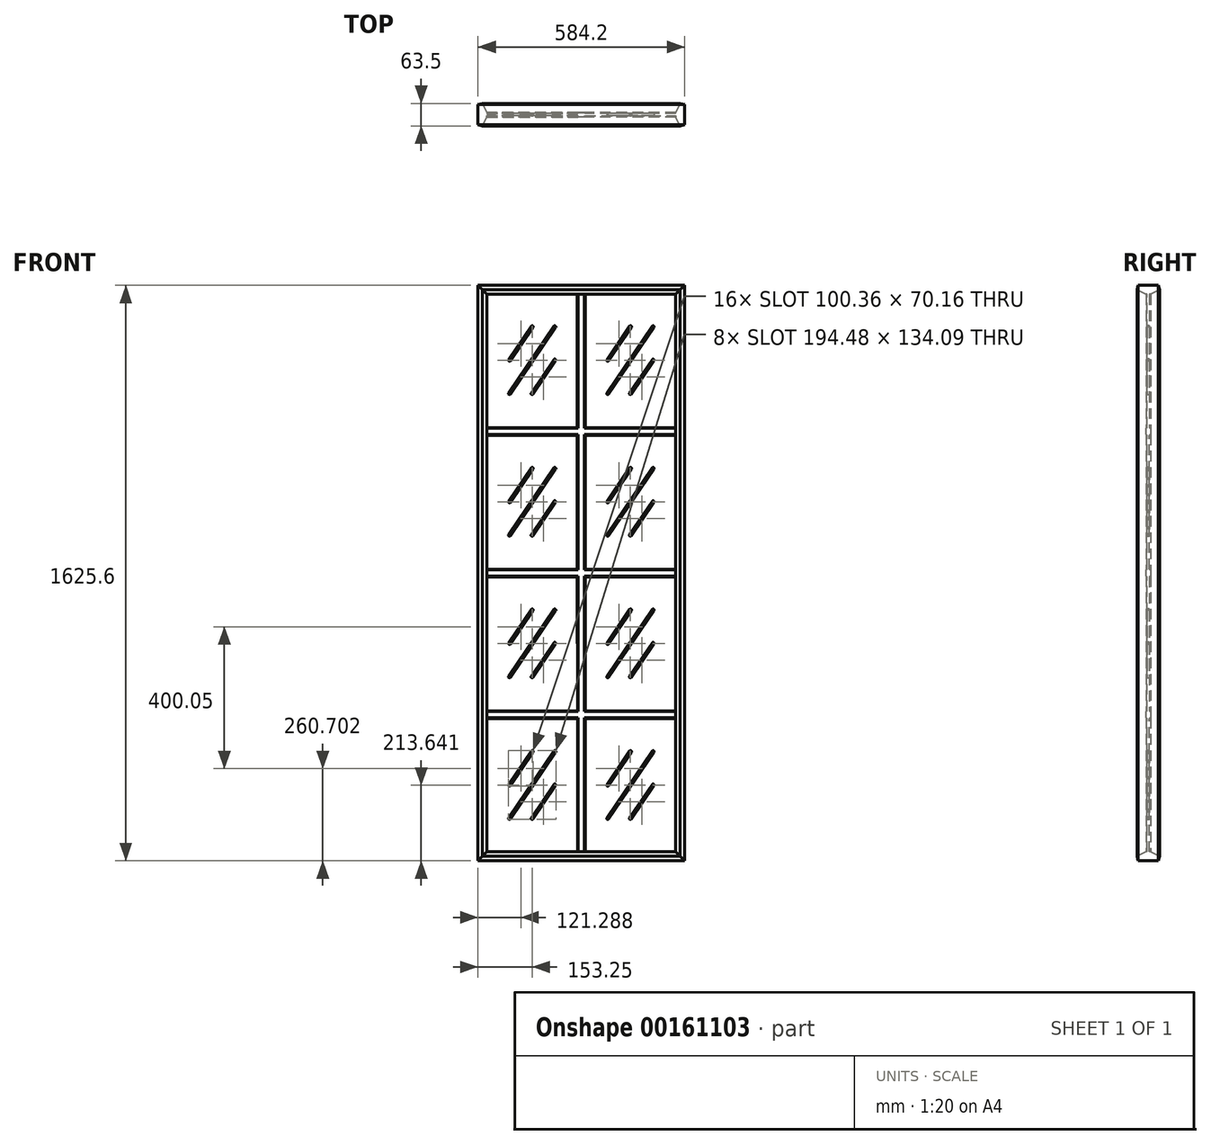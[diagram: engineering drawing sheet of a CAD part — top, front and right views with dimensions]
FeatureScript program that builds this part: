
annotation { "Feature Type Name" : "Feature", "Feature Type Description" : "" }
export const myFeature = defineFeature(function(context is Context, id is Id, definition is map)
    precondition{}
    {
        {
            var Q0;
            Q0=qCreatedBy(makeId("Front.planeOp"),FACE);
            var sketch = newSketch(context, id + "F0", { "sketchPlane" : qUnion([Q0])});
            skLineSegment(sketch, "E0.bottom", {"start": v(292.1, 812.8) * mm, "end": v(-292.1, 812.8) * mm});
            skLineSegment(sketch, "E0.top", {"start": v(292.1, -812.8) * mm, "end": v(-292.1, -812.8) * mm});
            skLineSegment(sketch, "E0.left", {"start": v(292.1, 812.8) * mm, "end": v(292.1, -812.8) * mm});
            skLineSegment(sketch, "E0.right", {"start": v(-292.1, 812.8) * mm, "end": v(-292.1, -812.8) * mm});
            skPoint(sketch, "E0.middle", {"position": v(0, 0) * mm});
            skSolve(sketch);
        }
        {
            var Q0;
            Q0 = qSketchRegion(id + "F0", true);
            var Q1;
            Q1 = qConstructionFilter(qBodyType(qCreatedBy(id + "F0" ,EDGE), BodyType.WIRE), ConstructionObject.NO);
            extrude(context, id + "F1", {"entities" : qUnion([Q0]), "bodyType" : ToolBodyType.SURFACE, "surfaceEntities" : qUnion([Q1]), "depth" : 28.57 * mm, "hasSecondDirection" : true, "secondDirectionOppositeDirection" : true, "secondDirectionDepth" : 28.57 * mm});
        }
        {
            var Q0;
            Q0=qCreatedBy(makeId("Front.planeOp"),FACE);
            var sketch = newSketch(context, id + "F2", { "sketchPlane" : qUnion([Q0])});
            skLineSegment(sketch, "E1.bottom", {"start": v(279.4, 800.1) * mm, "end": v(-279.4, 800.1) * mm});
            skLineSegment(sketch, "E1.top", {"start": v(279.4, -800.1) * mm, "end": v(-279.4, -800.1) * mm});
            skLineSegment(sketch, "E1.left", {"start": v(279.4, 800.1) * mm, "end": v(279.4, -800.1) * mm});
            skLineSegment(sketch, "E1.right", {"start": v(-279.4, 800.1) * mm, "end": v(-279.4, -800.1) * mm});
            skPoint(sketch, "E1.middle", {"position": v(0, 0) * mm});
            skSolve(sketch);
        }
        {
            var Q0;
            Q0 = qSketchRegion(id + "F2", true);
            var Q1;
            Q1 = qConstructionFilter(qBodyType(qCreatedBy(id + "F2" ,EDGE), BodyType.WIRE), ConstructionObject.NO);
            extrude(context, id + "F3", {"entities" : qUnion([Q0]), "bodyType" : ToolBodyType.SURFACE, "surfaceEntities" : qUnion([Q1]), "depth" : 31.75 * mm, "hasSecondDirection" : true, "secondDirectionOppositeDirection" : true, "secondDirectionDepth" : 31.75 * mm});
        }
        {
            var Q0;
            Q0=makeQuery(id+"F1.opExtrude","SWEPT_FACE",FACE,{"disambiguationData":[OSD([sQuery(id+"F0.wireOp",EDGE,"E0.bottom")])]});
            var Q1;
            Q1=makeQuery(id+"F3.opExtrude","SWEPT_FACE",FACE,{"disambiguationData":[OSD([sQuery(id+"F2.wireOp",EDGE,"E1.bottom")])]});
            loft(context, id + "F4", {"sheetProfilesArray" : [{ "sheetProfileEntities" : qUnion([Q0]) }, { "sheetProfileEntities" : qUnion([Q1]) }]});
        }
        {
            var Q1;
            Q1=makeQuery(id+"F1.opExtrude","SWEPT_FACE",FACE,{"disambiguationData":[OSD([sQuery(id+"F0.wireOp",EDGE,"E0.right")])]});
            var Q2;
            Q2=makeQuery(id+"F3.opExtrude","SWEPT_FACE",FACE,{"disambiguationData":[OSD([sQuery(id+"F2.wireOp",EDGE,"E1.right")])]});
            loft(context, id + "F5", {"operationType" : NewBodyOperationType.ADD, "sheetProfilesArray" : [{ "sheetProfileEntities" : qUnion([Q1]) }, { "sheetProfileEntities" : qUnion([Q2]) }]});
        }
        {
            var Q1;
            Q1=makeQuery(id+"F3.opExtrude","SWEPT_FACE",FACE,{"disambiguationData":[OSD([sQuery(id+"F2.wireOp",EDGE,"E1.left")])]});
            var Q2;
            Q2=makeQuery(id+"F1.opExtrude","SWEPT_FACE",FACE,{"disambiguationData":[OSD([sQuery(id+"F0.wireOp",EDGE,"E0.left")])]});
            loft(context, id + "F6", {"operationType" : NewBodyOperationType.ADD, "sheetProfilesArray" : [{ "sheetProfileEntities" : qUnion([Q1]) }, { "sheetProfileEntities" : qUnion([Q2]) }]});
        }
        {
            var Q1;
            Q1=makeQuery(id+"F3.opExtrude","SWEPT_FACE",FACE,{"disambiguationData":[OSD([sQuery(id+"F2.wireOp",EDGE,"E1.top")])]});
            var Q2;
            Q2=makeQuery(id+"F1.opExtrude","SWEPT_FACE",FACE,{"disambiguationData":[OSD([sQuery(id+"F0.wireOp",EDGE,"E0.top")])]});
            loft(context, id + "F7", {"operationType" : NewBodyOperationType.ADD, "sheetProfilesArray" : [{ "sheetProfileEntities" : qUnion([Q1]) }, { "sheetProfileEntities" : qUnion([Q2]) }]});
        }
        {
            var Q0;
            Q0=qCreatedBy(makeId("Front.planeOp"),FACE);
            var sketch = newSketch(context, id + "F8", { "sketchPlane" : qUnion([Q0])});
            skLineSegment(sketch, "E2.bottom", {"start": v(266.7, 787.4) * mm, "end": v(-266.7, 787.4) * mm});
            skLineSegment(sketch, "E2.top", {"start": v(266.7, -787.4) * mm, "end": v(-266.7, -787.4) * mm});
            skLineSegment(sketch, "E2.left", {"start": v(266.7, 787.4) * mm, "end": v(266.7, -787.4) * mm});
            skLineSegment(sketch, "E2.right", {"start": v(-266.7, 787.4) * mm, "end": v(-266.7, -787.4) * mm});
            skPoint(sketch, "E2.middle", {"position": v(0, 0) * mm});
            skSolve(sketch);
        }
        {
            var Q0;
            Q0 = qSketchRegion(id + "F8", true);
            var Q1;
            Q1 = qConstructionFilter(qBodyType(qCreatedBy(id + "F8" ,EDGE), BodyType.WIRE), ConstructionObject.NO);
            extrude(context, id + "F9", {"entities" : qUnion([Q0]), "bodyType" : ToolBodyType.SURFACE, "surfaceEntities" : qUnion([Q1]), "depth" : 6.35 * mm, "hasSecondDirection" : true, "secondDirectionOppositeDirection" : true, "secondDirectionDepth" : 6.35 * mm});
        }
        {
            var Q1;
            Q1=makeQuery(id+"F3.opExtrude","SWEPT_FACE",FACE,{"disambiguationData":[OSD([sQuery(id+"F2.wireOp",EDGE,"E1.bottom")])]});
            var Q2;
            Q2=makeQuery(id+"F9.opExtrude","SWEPT_FACE",FACE,{"disambiguationData":[OSD([sQuery(id+"F8.wireOp",EDGE,"E2.bottom")])]});
            loft(context, id + "F10", {"operationType" : NewBodyOperationType.ADD, "sheetProfilesArray" : [{ "sheetProfileEntities" : qUnion([Q1]) }, { "sheetProfileEntities" : qUnion([Q2]) }]});
        }
        {
            var Q1;
            Q1=makeQuery(id+"F9.opExtrude","SWEPT_FACE",FACE,{"disambiguationData":[OSD([sQuery(id+"F8.wireOp",EDGE,"E2.right")])]});
            var Q2;
            Q2=makeQuery(id+"F3.opExtrude","SWEPT_FACE",FACE,{"disambiguationData":[OSD([sQuery(id+"F2.wireOp",EDGE,"E1.right")])]});
            loft(context, id + "F11", {"operationType" : NewBodyOperationType.ADD, "sheetProfilesArray" : [{ "sheetProfileEntities" : qUnion([Q1]) }, { "sheetProfileEntities" : qUnion([Q2]) }]});
        }
        {
            var Q1;
            Q1=makeQuery(id+"F3.opExtrude","SWEPT_FACE",FACE,{"disambiguationData":[OSD([sQuery(id+"F2.wireOp",EDGE,"E1.left")])]});
            var Q2;
            Q2=makeQuery(id+"F9.opExtrude","SWEPT_FACE",FACE,{"disambiguationData":[OSD([sQuery(id+"F8.wireOp",EDGE,"E2.left")])]});
            loft(context, id + "F12", {"operationType" : NewBodyOperationType.ADD, "sheetProfilesArray" : [{ "sheetProfileEntities" : qUnion([Q1]) }, { "sheetProfileEntities" : qUnion([Q2]) }]});
        }
        {
            var Q1;
            Q1=makeQuery(id+"F3.opExtrude","SWEPT_FACE",FACE,{"disambiguationData":[OSD([sQuery(id+"F2.wireOp",EDGE,"E1.top")])]});
            var Q2;
            Q2=makeQuery(id+"F9.opExtrude","SWEPT_FACE",FACE,{"disambiguationData":[OSD([sQuery(id+"F8.wireOp",EDGE,"E2.top")])]});
            loft(context, id + "F13", {"operationType" : NewBodyOperationType.ADD, "sheetProfilesArray" : [{ "sheetProfileEntities" : qUnion([Q1]) }, { "sheetProfileEntities" : qUnion([Q2]) }]});
        }
        {
            var Q0;
            Q0=qCreatedBy(makeId("Front.planeOp"),FACE);
            var sketch = newSketch(context, id + "F14", { "sketchPlane" : qUnion([Q0])});
            skLineSegment(sketch, "E3.0.0", {"start": v(-266.7, 787.4) * mm, "end": v(266.7, 787.4) * mm});
            skLineSegment(sketch, "E3.0.2", {"start": v(-266.7, 787.4) * mm, "end": v(266.7, 787.4) * mm});
            skLineSegment(sketch, "E4.0.0", {"start": v(266.7, -787.4) * mm, "end": v(266.7, 787.4) * mm});
            skLineSegment(sketch, "E4.0.2", {"start": v(266.7, 787.4) * mm, "end": v(266.7, -787.4) * mm});
            skLineSegment(sketch, "E5.0.0", {"start": v(-266.7, -787.4) * mm, "end": v(-266.7, 787.4) * mm});
            skLineSegment(sketch, "E5.0.2", {"start": v(-266.7, -787.4) * mm, "end": v(-266.7, 787.4) * mm});
            skLineSegment(sketch, "E6.0.0", {"start": v(-266.7, -787.4) * mm, "end": v(266.7, -787.4) * mm});
            skLineSegment(sketch, "E6.0.2", {"start": v(266.7, -787.4) * mm, "end": v(-266.7, -787.4) * mm});
            skSolve(sketch);
        }
        {
            var Q0;
            Q0 = qSketchRegion(id + "F14", true);
            extrude(context, id + "F15", {"entities" : qUnion([Q0]), "operationType" : NewBodyOperationType.ADD, "depth" : 3.17 * mm, "hasSecondDirection" : true, "secondDirectionOppositeDirection" : true, "secondDirectionDepth" : 3.17 * mm});
        }
        {
            var Q0;
            Q0=qCreatedBy(makeId("Front.planeOp"),FACE);
            var sketch = newSketch(context, id + "F16", { "sketchPlane" : qUnion([Q0])});
            skLineSegment(sketch, "E7", {"start": v(0, -796.3) * mm, "end": v(-12.7, -796.3) * mm});
            skLineSegment(sketch, "E8", {"start": v(-12.7, -796.3) * mm, "end": v(-13.25, 796.46) * mm});
            skLineSegment(sketch, "E9", {"start": v(-13.25, 796.46) * mm, "end": v(-0.76, 796.46) * mm});
            skLineSegment(sketch, "E10", {"start": v(-0.76, 796.46) * mm, "end": v(12.7, 796.46) * mm});
            skLineSegment(sketch, "E11", {"start": v(12.7, 796.46) * mm, "end": v(12.7, -796.3) * mm});
            skLineSegment(sketch, "E12", {"start": v(12.7, -796.3) * mm, "end": v(0, -796.3) * mm});
            skSolve(sketch);
        }
        {
            var Q0;
            Q0 = qSketchRegion(id + "F16", true);
            extrude(context, id + "F17", {"entities" : qUnion([Q0]), "operationType" : NewBodyOperationType.ADD, "depth" : 6.35 * mm, "hasDraft" : true, "draftAngle" : 30 * degree, "draftPullDirection" : true, "hasSecondDirection" : true, "secondDirectionOppositeDirection" : true, "secondDirectionDepth" : 6.35 * mm, "hasSecondDirectionDraft" : true, "secondDirectionDraftAngle" : 30 * degree, "secondDirectionDraftPullDirection" : true});
        }
        {
            var Q0;
            Q0=qCreatedBy(makeId("Front.planeOp"),FACE);
            var sketch = newSketch(context, id + "F18", { "sketchPlane" : qUnion([Q0])});
            skLineSegment(sketch, "E13", {"start": v(-282.62, -412.75) * mm, "end": v(-282.62, -387.35) * mm});
            skLineSegment(sketch, "E14", {"start": v(-282.62, -387.35) * mm, "end": v(278.66, -387.35) * mm});
            skLineSegment(sketch, "E15", {"start": v(278.66, -387.35) * mm, "end": v(278.66, -412.75) * mm});
            skLineSegment(sketch, "E16", {"start": v(278.66, -412.75) * mm, "end": v(-282.62, -412.75) * mm});
            skLineSegment(sketch, "E17", {"start": v(-282.62, 12.7) * mm, "end": v(-282.62, -12.7) * mm});
            skLineSegment(sketch, "E18", {"start": v(-282.62, -12.7) * mm, "end": v(278.66, -12.7) * mm});
            skLineSegment(sketch, "E19", {"start": v(278.66, -12.7) * mm, "end": v(278.66, 12.7) * mm});
            skLineSegment(sketch, "E20", {"start": v(278.66, 12.7) * mm, "end": v(-282.62, 12.7) * mm});
            skLineSegment(sketch, "E21", {"start": v(-282.62, -387.35) * mm, "end": v(-282.62, -412.75) * mm});
            skLineSegment(sketch, "E22", {"start": v(-282.62, 387.35) * mm, "end": v(-282.62, 412.75) * mm});
            skLineSegment(sketch, "E23", {"start": v(-282.62, 412.75) * mm, "end": v(278.66, 412.75) * mm});
            skLineSegment(sketch, "E24", {"start": v(278.66, 412.75) * mm, "end": v(278.66, 387.35) * mm});
            skLineSegment(sketch, "E25", {"start": v(278.66, 387.35) * mm, "end": v(-282.62, 387.35) * mm});
            skSolve(sketch);
        }
        {
            var Q0;
            Q0 = qSketchRegion(id + "F18", true);
            extrude(context, id + "F19", {"entities" : qUnion([Q0]), "operationType" : NewBodyOperationType.ADD, "depth" : 6.35 * mm, "hasDraft" : true, "draftAngle" : 30 * degree, "draftPullDirection" : true, "hasSecondDirection" : true, "secondDirectionOppositeDirection" : true, "secondDirectionDepth" : 6.35 * mm, "hasSecondDirectionDraft" : true, "secondDirectionDraftAngle" : 30 * degree, "secondDirectionDraftPullDirection" : true});
        }
        {
            var Q0;
            Q0=qCreatedBy(makeId("Front.planeOp"),FACE);
            var sketch = newSketch(context, id + "F20", { "sketchPlane" : qUnion([Q0])});
            skLineSegment(sketch, "E26.0.0", {"start": v(-11, -410.92) * mm, "end": v(-266.7, -410.92) * mm});
            skLineSegment(sketch, "E26.0.1", {"start": v(-266.7, -410.92) * mm, "end": v(-266.7, -787.4) * mm});
            skLineSegment(sketch, "E26.0.2", {"start": v(-266.7, -787.4) * mm, "end": v(-10.87, -787.4) * mm});
            skLineSegment(sketch, "E26.0.3", {"start": v(-10.87, -787.4) * mm, "end": v(-11, -410.92) * mm});
            skLineSegment(sketch, "E27", {"start": v(-11, -410.92) * mm, "end": v(-74.92, -505.04) * mm});
            skLineSegment(sketch, "E28", {"start": v(-202.77, -693.28) * mm, "end": v(-266.7, -787.4) * mm});
            skLineSegment(sketch, "E29", {"start": v(-202.77, -693.28) * mm, "end": v(-138.85, -599.16) * mm});
            skLineSegment(sketch, "E30", {"start": v(-74.92, -505.04) * mm, "end": v(-138.85, -599.16) * mm});
            skLineSegment(sketch, "E31", {"start": v(-138.85, -599.16) * mm, "end": v(-138.85, -505.04) * mm});
            skLineSegment(sketch, "E32", {"start": v(-138.85, -599.16) * mm, "end": v(-138.85, -693.28) * mm});
            skLineSegment(sketch, "E33", {"start": v(-138.85, -599.16) * mm, "end": v(-74.92, -599.16) * mm});
            skLineSegment(sketch, "E34", {"start": v(-138.85, -599.16) * mm, "end": v(-202.77, -599.16) * mm});
            skLineSegment(sketch, "E35", {"start": v(-74.92, -599.16) * mm, "end": v(-138.85, -693.28) * mm});
            skLineSegment(sketch, "E36", {"start": v(-138.85, -505.04) * mm, "end": v(-202.77, -599.16) * mm});
            skLineSegment(sketch, "E37.0.0", {"start": v(266.7, -410.92) * mm, "end": v(10.87, -410.92) * mm});
            skLineSegment(sketch, "E37.0.1", {"start": v(10.87, -410.92) * mm, "end": v(10.87, -787.4) * mm});
            skLineSegment(sketch, "E37.0.2", {"start": v(10.87, -787.4) * mm, "end": v(266.7, -787.4) * mm});
            skLineSegment(sketch, "E37.0.3", {"start": v(266.7, -787.4) * mm, "end": v(266.7, -410.92) * mm});
            skLineSegment(sketch, "E38.0.0", {"start": v(-11, -389.18) * mm, "end": v(-11.14, -10.87) * mm});
            skLineSegment(sketch, "E38.0.1", {"start": v(-11.14, -10.87) * mm, "end": v(-266.7, -10.87) * mm});
            skLineSegment(sketch, "E38.0.2", {"start": v(-266.7, -10.87) * mm, "end": v(-266.7, -389.18) * mm});
            skLineSegment(sketch, "E38.0.3", {"start": v(-266.7, -389.18) * mm, "end": v(-11, -389.18) * mm});
            skSolve(sketch);
        }
        {
            var Q0;
            Q0=qCreatedBy(makeId("Front.planeOp"),FACE);
            var sketch = newSketch(context, id + "F21", { "sketchPlane" : qUnion([Q0])});
            skLineSegment(sketch, "E39.RBB1.RBB1", {"start": v(-138.85, -505.04) * mm, "end": v(-202.77, -599.16) * mm, "construction": true});
            skArc(sketch, "E39.0.startCap", {"start": v(-141.48, -503.25) * mm, "mid": v(-137.07, -502.41) * mm, "end": v(-136.22, -506.82) * mm});
            skArc(sketch, "E39.0.endCap", {"start": v(-200.15, -600.94) * mm, "mid": v(-204.56, -601.78) * mm, "end": v(-205.4, -597.37) * mm});
            skLineSegment(sketch, "E39.0.left", {"start": v(-136.22, -506.82) * mm, "end": v(-200.15, -600.94) * mm});
            skLineSegment(sketch, "E39.0.right", {"start": v(-141.48, -503.25) * mm, "end": v(-205.4, -597.37) * mm});
            skPoint(sketch, "E40.0", {"position": v(-74.92, -505.04) * mm});
            skPoint(sketch, "E41.0", {"position": v(-202.77, -693.28) * mm});
            skLineSegment(sketch, "E42", {"start": v(-74.92, -505.04) * mm, "end": v(-202.77, -693.28) * mm});
            skLineSegment(sketch, "E43.RBBx.RBBx", {"start": v(-74.92, -599.16) * mm, "end": v(-138.85, -693.28) * mm, "construction": true});
            skArc(sketch, "E43.0.startCap", {"start": v(-77.55, -597.37) * mm, "mid": v(-73.14, -596.53) * mm, "end": v(-72.3, -600.94) * mm});
            skArc(sketch, "E43.0.endCap", {"start": v(-136.22, -695.06) * mm, "mid": v(-140.63, -695.9) * mm, "end": v(-141.48, -691.5) * mm});
            skLineSegment(sketch, "E43.0.left", {"start": v(-72.3, -600.94) * mm, "end": v(-136.22, -695.06) * mm});
            skLineSegment(sketch, "E43.0.right", {"start": v(-77.55, -597.37) * mm, "end": v(-141.48, -691.5) * mm});
            skArc(sketch, "E44.0.startCap", {"start": v(-77.55, -503.25) * mm, "mid": v(-73.14, -502.41) * mm, "end": v(-72.3, -506.82) * mm});
            skArc(sketch, "E44.0.endCap", {"start": v(-200.15, -695.06) * mm, "mid": v(-204.56, -695.9) * mm, "end": v(-205.4, -691.5) * mm});
            skLineSegment(sketch, "E44.0.left", {"start": v(-72.3, -506.82) * mm, "end": v(-200.15, -695.06) * mm});
            skLineSegment(sketch, "E44.0.right", {"start": v(-77.55, -503.25) * mm, "end": v(-205.4, -691.5) * mm});
            skPoint(sketch, "E45.0", {"position": v(-11.14, -10.87) * mm});
            skPoint(sketch, "E46.0", {"position": v(-11, -410.92) * mm});
            skPoint(sketch, "E47.0", {"position": v(266.7, -410.92) * mm});
            skArc(sketch, "E48.0.1.0", {"start": v(-200.15, -200.9) * mm, "mid": v(-204.56, -201.73) * mm, "end": v(-205.4, -197.32) * mm});
            skLineSegment(sketch, "E48.0.1.1", {"start": v(-136.22, -106.77) * mm, "end": v(-200.15, -200.9) * mm});
            skArc(sketch, "E48.0.1.2", {"start": v(-141.48, -103.2) * mm, "mid": v(-137.07, -102.36) * mm, "end": v(-136.22, -106.77) * mm});
            skLineSegment(sketch, "E48.0.1.3", {"start": v(-141.48, -103.2) * mm, "end": v(-205.4, -197.32) * mm});
            skLineSegment(sketch, "E48.0.1.4", {"start": v(-77.55, -103.2) * mm, "end": v(-205.4, -291.45) * mm});
            skArc(sketch, "E48.0.1.5", {"start": v(-200.15, -295.01) * mm, "mid": v(-204.56, -295.86) * mm, "end": v(-205.4, -291.45) * mm});
            skLineSegment(sketch, "E48.0.1.6", {"start": v(-72.3, -106.77) * mm, "end": v(-200.15, -295.01) * mm});
            skArc(sketch, "E48.0.1.7", {"start": v(-77.55, -103.2) * mm, "mid": v(-73.14, -102.36) * mm, "end": v(-72.3, -106.77) * mm});
            skArc(sketch, "E48.0.1.8", {"start": v(-77.55, -197.32) * mm, "mid": v(-73.14, -196.48) * mm, "end": v(-72.3, -200.9) * mm});
            skLineSegment(sketch, "E48.0.1.9", {"start": v(-72.3, -200.9) * mm, "end": v(-136.22, -295.01) * mm});
            skArc(sketch, "E48.0.1.10", {"start": v(-136.22, -295.01) * mm, "mid": v(-140.63, -295.86) * mm, "end": v(-141.48, -291.45) * mm});
            skLineSegment(sketch, "E48.0.1.11", {"start": v(-77.55, -197.32) * mm, "end": v(-141.48, -291.45) * mm});
            skArc(sketch, "E48.0.2.0", {"start": v(-200.15, 199.16) * mm, "mid": v(-204.56, 198.32) * mm, "end": v(-205.4, 202.73) * mm});
            skLineSegment(sketch, "E48.0.2.1", {"start": v(-136.22, 293.28) * mm, "end": v(-200.15, 199.16) * mm});
            skArc(sketch, "E48.0.2.2", {"start": v(-141.48, 296.85) * mm, "mid": v(-137.07, 297.69) * mm, "end": v(-136.22, 293.28) * mm});
            skLineSegment(sketch, "E48.0.2.3", {"start": v(-141.48, 296.85) * mm, "end": v(-205.4, 202.73) * mm});
            skLineSegment(sketch, "E48.0.2.4", {"start": v(-77.55, 296.85) * mm, "end": v(-205.4, 108.6) * mm});
            skArc(sketch, "E48.0.2.5", {"start": v(-200.15, 105.04) * mm, "mid": v(-204.56, 104.2) * mm, "end": v(-205.4, 108.6) * mm});
            skLineSegment(sketch, "E48.0.2.6", {"start": v(-72.3, 293.28) * mm, "end": v(-200.15, 105.04) * mm});
            skArc(sketch, "E48.0.2.7", {"start": v(-77.55, 296.85) * mm, "mid": v(-73.14, 297.69) * mm, "end": v(-72.3, 293.28) * mm});
            skArc(sketch, "E48.0.2.8", {"start": v(-77.55, 202.73) * mm, "mid": v(-73.14, 203.57) * mm, "end": v(-72.3, 199.16) * mm});
            skLineSegment(sketch, "E48.0.2.9", {"start": v(-72.3, 199.16) * mm, "end": v(-136.22, 105.04) * mm});
            skArc(sketch, "E48.0.2.10", {"start": v(-136.22, 105.04) * mm, "mid": v(-140.63, 104.2) * mm, "end": v(-141.48, 108.6) * mm});
            skLineSegment(sketch, "E48.0.2.11", {"start": v(-77.55, 202.73) * mm, "end": v(-141.48, 108.6) * mm});
            skArc(sketch, "E48.0.3.0", {"start": v(-200.15, 599.2) * mm, "mid": v(-204.56, 598.37) * mm, "end": v(-205.4, 602.78) * mm});
            skLineSegment(sketch, "E48.0.3.1", {"start": v(-136.22, 693.33) * mm, "end": v(-200.15, 599.2) * mm});
            skArc(sketch, "E48.0.3.2", {"start": v(-141.48, 696.9) * mm, "mid": v(-137.07, 697.74) * mm, "end": v(-136.22, 693.33) * mm});
            skLineSegment(sketch, "E48.0.3.3", {"start": v(-141.48, 696.9) * mm, "end": v(-205.4, 602.78) * mm});
            skLineSegment(sketch, "E48.0.3.4", {"start": v(-77.55, 696.9) * mm, "end": v(-205.4, 508.65) * mm});
            skArc(sketch, "E48.0.3.5", {"start": v(-200.15, 505.09) * mm, "mid": v(-204.56, 504.24) * mm, "end": v(-205.4, 508.65) * mm});
            skLineSegment(sketch, "E48.0.3.6", {"start": v(-72.3, 693.33) * mm, "end": v(-200.15, 505.09) * mm});
            skArc(sketch, "E48.0.3.7", {"start": v(-77.55, 696.9) * mm, "mid": v(-73.14, 697.74) * mm, "end": v(-72.3, 693.33) * mm});
            skArc(sketch, "E48.0.3.8", {"start": v(-77.55, 602.78) * mm, "mid": v(-73.14, 603.62) * mm, "end": v(-72.3, 599.2) * mm});
            skLineSegment(sketch, "E48.0.3.9", {"start": v(-72.3, 599.2) * mm, "end": v(-136.22, 505.09) * mm});
            skArc(sketch, "E48.0.3.10", {"start": v(-136.22, 505.09) * mm, "mid": v(-140.63, 504.24) * mm, "end": v(-141.48, 508.65) * mm});
            skLineSegment(sketch, "E48.0.3.11", {"start": v(-77.55, 602.78) * mm, "end": v(-141.48, 508.65) * mm});
            skArc(sketch, "E48.1.0.0", {"start": v(77.55, -600.94) * mm, "mid": v(73.14, -601.78) * mm, "end": v(72.3, -597.37) * mm});
            skLineSegment(sketch, "E48.1.0.1", {"start": v(141.48, -506.82) * mm, "end": v(77.55, -600.94) * mm});
            skArc(sketch, "E48.1.0.2", {"start": v(136.22, -503.25) * mm, "mid": v(140.63, -502.41) * mm, "end": v(141.48, -506.82) * mm});
            skLineSegment(sketch, "E48.1.0.3", {"start": v(136.22, -503.25) * mm, "end": v(72.3, -597.37) * mm});
            skLineSegment(sketch, "E48.1.0.4", {"start": v(200.15, -503.25) * mm, "end": v(72.3, -691.5) * mm});
            skArc(sketch, "E48.1.0.5", {"start": v(77.55, -695.06) * mm, "mid": v(73.14, -695.9) * mm, "end": v(72.3, -691.5) * mm});
            skLineSegment(sketch, "E48.1.0.6", {"start": v(205.4, -506.82) * mm, "end": v(77.55, -695.06) * mm});
            skArc(sketch, "E48.1.0.7", {"start": v(200.15, -503.25) * mm, "mid": v(204.56, -502.41) * mm, "end": v(205.4, -506.82) * mm});
            skArc(sketch, "E48.1.0.8", {"start": v(200.15, -597.37) * mm, "mid": v(204.56, -596.53) * mm, "end": v(205.4, -600.94) * mm});
            skLineSegment(sketch, "E48.1.0.9", {"start": v(205.4, -600.94) * mm, "end": v(141.48, -695.06) * mm});
            skArc(sketch, "E48.1.0.10", {"start": v(141.48, -695.06) * mm, "mid": v(137.07, -695.9) * mm, "end": v(136.22, -691.5) * mm});
            skLineSegment(sketch, "E48.1.0.11", {"start": v(200.15, -597.37) * mm, "end": v(136.22, -691.5) * mm});
            skArc(sketch, "E48.1.1.0", {"start": v(77.55, -200.9) * mm, "mid": v(73.14, -201.73) * mm, "end": v(72.3, -197.32) * mm});
            skLineSegment(sketch, "E48.1.1.1", {"start": v(141.48, -106.77) * mm, "end": v(77.55, -200.9) * mm});
            skArc(sketch, "E48.1.1.2", {"start": v(136.22, -103.2) * mm, "mid": v(140.63, -102.36) * mm, "end": v(141.48, -106.77) * mm});
            skLineSegment(sketch, "E48.1.1.3", {"start": v(136.22, -103.2) * mm, "end": v(72.3, -197.32) * mm});
            skLineSegment(sketch, "E48.1.1.4", {"start": v(200.15, -103.2) * mm, "end": v(72.3, -291.45) * mm});
            skArc(sketch, "E48.1.1.5", {"start": v(77.55, -295.01) * mm, "mid": v(73.14, -295.86) * mm, "end": v(72.3, -291.45) * mm});
            skLineSegment(sketch, "E48.1.1.6", {"start": v(205.4, -106.77) * mm, "end": v(77.55, -295.01) * mm});
            skArc(sketch, "E48.1.1.7", {"start": v(200.15, -103.2) * mm, "mid": v(204.56, -102.36) * mm, "end": v(205.4, -106.77) * mm});
            skArc(sketch, "E48.1.1.8", {"start": v(200.15, -197.32) * mm, "mid": v(204.56, -196.48) * mm, "end": v(205.4, -200.9) * mm});
            skLineSegment(sketch, "E48.1.1.9", {"start": v(205.4, -200.9) * mm, "end": v(141.48, -295.01) * mm});
            skArc(sketch, "E48.1.1.10", {"start": v(141.48, -295.01) * mm, "mid": v(137.07, -295.86) * mm, "end": v(136.22, -291.45) * mm});
            skLineSegment(sketch, "E48.1.1.11", {"start": v(200.15, -197.32) * mm, "end": v(136.22, -291.45) * mm});
            skArc(sketch, "E48.1.2.0", {"start": v(77.55, 199.16) * mm, "mid": v(73.14, 198.32) * mm, "end": v(72.3, 202.73) * mm});
            skLineSegment(sketch, "E48.1.2.1", {"start": v(141.48, 293.28) * mm, "end": v(77.55, 199.16) * mm});
            skArc(sketch, "E48.1.2.2", {"start": v(136.22, 296.85) * mm, "mid": v(140.63, 297.69) * mm, "end": v(141.48, 293.28) * mm});
            skLineSegment(sketch, "E48.1.2.3", {"start": v(136.22, 296.85) * mm, "end": v(72.3, 202.73) * mm});
            skLineSegment(sketch, "E48.1.2.4", {"start": v(200.15, 296.85) * mm, "end": v(72.3, 108.6) * mm});
            skArc(sketch, "E48.1.2.5", {"start": v(77.55, 105.04) * mm, "mid": v(73.14, 104.2) * mm, "end": v(72.3, 108.6) * mm});
            skLineSegment(sketch, "E48.1.2.6", {"start": v(205.4, 293.28) * mm, "end": v(77.55, 105.04) * mm});
            skArc(sketch, "E48.1.2.7", {"start": v(200.15, 296.85) * mm, "mid": v(204.56, 297.69) * mm, "end": v(205.4, 293.28) * mm});
            skArc(sketch, "E48.1.2.8", {"start": v(200.15, 202.73) * mm, "mid": v(204.56, 203.57) * mm, "end": v(205.4, 199.16) * mm});
            skLineSegment(sketch, "E48.1.2.9", {"start": v(205.4, 199.16) * mm, "end": v(141.48, 105.04) * mm});
            skArc(sketch, "E48.1.2.10", {"start": v(141.48, 105.04) * mm, "mid": v(137.07, 104.2) * mm, "end": v(136.22, 108.6) * mm});
            skLineSegment(sketch, "E48.1.2.11", {"start": v(200.15, 202.73) * mm, "end": v(136.22, 108.6) * mm});
            skArc(sketch, "E48.1.3.0", {"start": v(77.55, 599.2) * mm, "mid": v(73.14, 598.37) * mm, "end": v(72.3, 602.78) * mm});
            skLineSegment(sketch, "E48.1.3.1", {"start": v(141.48, 693.33) * mm, "end": v(77.55, 599.2) * mm});
            skArc(sketch, "E48.1.3.2", {"start": v(136.22, 696.9) * mm, "mid": v(140.63, 697.74) * mm, "end": v(141.48, 693.33) * mm});
            skLineSegment(sketch, "E48.1.3.3", {"start": v(136.22, 696.9) * mm, "end": v(72.3, 602.78) * mm});
            skLineSegment(sketch, "E48.1.3.4", {"start": v(200.15, 696.9) * mm, "end": v(72.3, 508.65) * mm});
            skArc(sketch, "E48.1.3.5", {"start": v(77.55, 505.09) * mm, "mid": v(73.14, 504.24) * mm, "end": v(72.3, 508.65) * mm});
            skLineSegment(sketch, "E48.1.3.6", {"start": v(205.4, 693.33) * mm, "end": v(77.55, 505.09) * mm});
            skArc(sketch, "E48.1.3.7", {"start": v(200.15, 696.9) * mm, "mid": v(204.56, 697.74) * mm, "end": v(205.4, 693.33) * mm});
            skArc(sketch, "E48.1.3.8", {"start": v(200.15, 602.78) * mm, "mid": v(204.56, 603.62) * mm, "end": v(205.4, 599.2) * mm});
            skLineSegment(sketch, "E48.1.3.9", {"start": v(205.4, 599.2) * mm, "end": v(141.48, 505.09) * mm});
            skArc(sketch, "E48.1.3.10", {"start": v(141.48, 505.09) * mm, "mid": v(137.07, 504.24) * mm, "end": v(136.22, 508.65) * mm});
            skLineSegment(sketch, "E48.1.3.11", {"start": v(200.15, 602.78) * mm, "end": v(136.22, 508.65) * mm});
            skLineSegment(sketch, "E48.direction1", {"start": v(-205.4, -691.5) * mm, "end": v(72.3, -691.5) * mm, "construction": true});
            skLineSegment(sketch, "E48.direction2", {"start": v(-205.4, -691.5) * mm, "end": v(-205.4, -291.45) * mm, "construction": true});
            skSolve(sketch);
        }
        {
            var Q0;
            Q0 = qSketchRegion(id + "F21", true);
            extrude(context, id + "F22", {"entities" : qUnion([Q0]), "operationType" : NewBodyOperationType.REMOVE, "endBound" : BoundingType.THROUGH_ALL, "oppositeDirection" : true, "depth" : 25.4 * mm, "hasSecondDirection" : true, "secondDirectionBound" : SecondDirectionBoundingType.THROUGH_ALL, "secondDirectionOppositeDirection" : false, "secondDirectionDepth" : 25.4 * mm});
        }
    });
